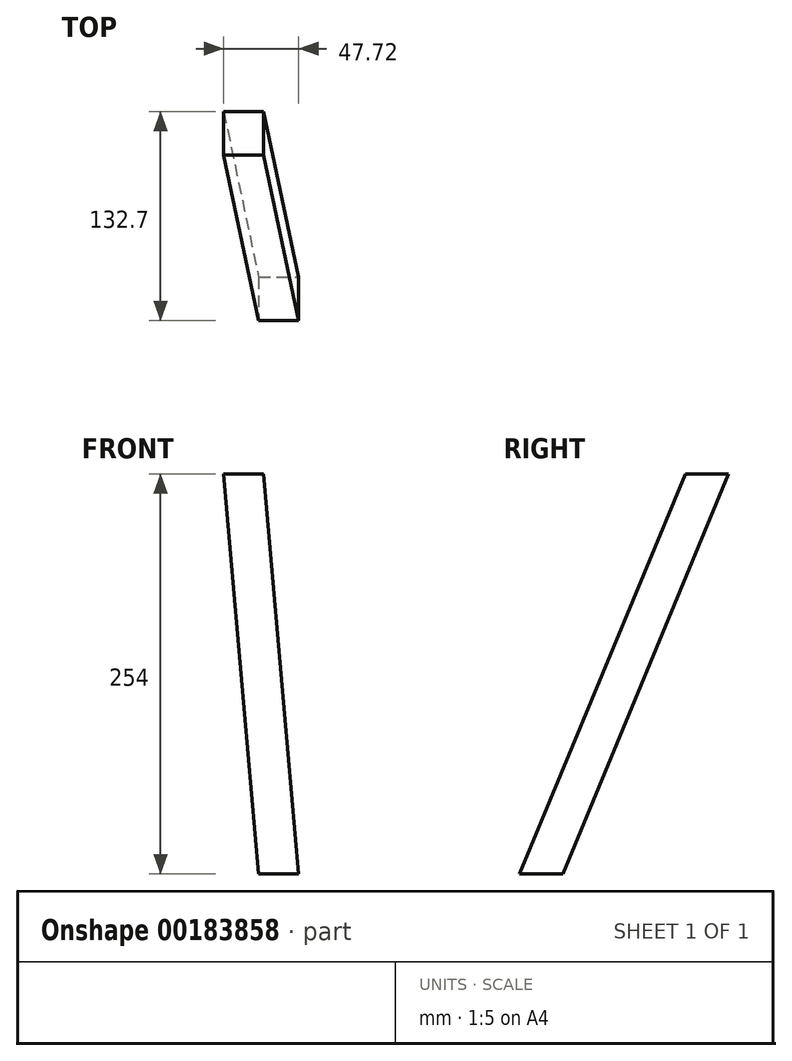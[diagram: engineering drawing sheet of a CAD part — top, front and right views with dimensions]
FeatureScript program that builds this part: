
annotation { "Feature Type Name" : "Feature", "Feature Type Description" : "" }
export const myFeature = defineFeature(function(context is Context, id is Id, definition is map)
    precondition{}
    {
        {
            var Q0;
            Q0=qCreatedBy(makeId("Front.planeOp"),FACE);
            var sketch = newSketch(context, id + "F0", { "sketchPlane" : qUnion([Q0])});
            skLineSegment(sketch, "E0.bottom", {"start": v(0, 0) * mm, "end": v(185.66, 0) * mm});
            skLineSegment(sketch, "E0.top", {"start": v(0, 254) * mm, "end": v(185.66, 254) * mm});
            skLineSegment(sketch, "E0.left", {"start": v(0, 0) * mm, "end": v(0, 254) * mm});
            skLineSegment(sketch, "E0.right", {"start": v(185.66, 0) * mm, "end": v(185.66, 254) * mm});
            skSolve(sketch);
        }
        {
            var Q0;
            Q0=makeQuery(id+"F0.imprint","IMPRINT",FACE,{"disambiguationData":[TD([[makeQuery(id+"F0.imprint","IMPRINT",EDGE,{"derivedFrom":sQuery(id+"F0.wireOp",EDGE,"E0.bottom")}),1.0]])]});
            extrude(context, id + "F1", {"entities" : qUnion([Q0]), "depth" : 254 * mm});
        }
        {
            var Q0;
            Q0=makeQuery(id+"F1.opExtrude","CAP_FACE",FACE,{"disambiguationData":[OSD([sQuery(id+"F0.wireOp",EDGE,"E0.bottom"),sQuery(id+"F0.wireOp",EDGE,"E0.top"),sQuery(id+"F0.wireOp",EDGE,"E0.left"),sQuery(id+"F0.wireOp",EDGE,"E0.right")])],"isStart":false});
            var sketch = newSketch(context, id + "F2", { "sketchPlane" : qUnion([Q0])});
            skLineSegment(sketch, "E1", {"start": v(0, 1743.05) * mm, "end": v(152.5, 0) * mm});
            skLineSegment(sketch, "E2", {"start": v(0, 1451.62) * mm, "end": v(127, 0) * mm});
            skSolve(sketch);
        }
        {
            var Q0;
            {var subQ5=makeQuery(id+"F1.opExtrude","CAP_EDGE",EDGE,{"disambiguationData":[OSD([sQuery(id+"F0.wireOp",EDGE,"E0.left")])],"isStart":false});Q0=makeQuery(id+"F2.imprint","IMPRINT",FACE,{"disambiguationData":[TD([[makeQuery(id+"F2.imprint","IMPRINT",EDGE,{"derivedFrom":subQ5}),-1.0]])]});}
            extrude(context, id + "F3", {"entities" : qUnion([Q0]), "operationType" : NewBodyOperationType.REMOVE, "endBound" : BoundingType.THROUGH_ALL, "oppositeDirection" : true, "depth" : 25.4 * mm});
        }
        {
            var Q0;
            Q0=makeQuery(id+"F1.opExtrude","SWEPT_FACE",FACE,{"disambiguationData":[OSD([sQuery(id+"F0.wireOp",EDGE,"E0.right")])]});
            var sketch = newSketch(context, id + "F4", { "sketchPlane" : qUnion([Q0])});
            skLineSegment(sketch, "E3", {"start": v(-254, 0) * mm, "end": v(-148.79, 254) * mm});
            skLineSegment(sketch, "E4", {"start": v(-226.5, 0) * mm, "end": v(-121.3, 254) * mm});
            skSolve(sketch);
        }
        {
            var Q0;
            {var subQ0=sQuery(id+"F4.wireOp",EDGE,"E3");Q0=makeQuery(id+"F4.imprint","IMPRINT",FACE,{"disambiguationData":[TD([[makeQuery(id+"F4.imprint","IMPRINT",EDGE,{"derivedFrom":subQ0}),1.0]])]});}
            extrude(context, id + "F5", {"entities" : qUnion([Q0]), "operationType" : NewBodyOperationType.REMOVE, "endBound" : BoundingType.THROUGH_ALL, "oppositeDirection" : true, "depth" : 25.4 * mm});
        }
        {
            var Q0;
            {var subQ0=sQuery(id+"F4.wireOp",EDGE,"E4");Q0=makeQuery(id+"F4.imprint","IMPRINT",FACE,{"disambiguationData":[TD([[makeQuery(id+"F4.imprint","IMPRINT",EDGE,{"derivedFrom":subQ0}),-1.0]])]});}
            extrude(context, id + "F6", {"entities" : qUnion([Q0]), "operationType" : NewBodyOperationType.REMOVE, "endBound" : BoundingType.THROUGH_ALL, "oppositeDirection" : true, "depth" : 25.4 * mm});
        }
        {
            var Q0;
            {var subQ5=makeQuery(id+"F1.opExtrude","CAP_EDGE",EDGE,{"disambiguationData":[OSD([sQuery(id+"F0.wireOp",EDGE,"E0.right")])],"isStart":false});Q0=makeQuery(id+"F2.imprint","IMPRINT",FACE,{"disambiguationData":[TD([[makeQuery(id+"F2.imprint","IMPRINT",EDGE,{"derivedFrom":subQ5}),1.0]])]});}
            extrude(context, id + "F7", {"entities" : qUnion([Q0]), "operationType" : NewBodyOperationType.REMOVE, "endBound" : BoundingType.THROUGH_ALL, "oppositeDirection" : true, "depth" : 25.4 * mm});
        }
        {
            var Q0;
            {var subQ0=sQuery(id+"F0.wireOp",EDGE,"E0.bottom");Q0=makeQuery(id+"F5.boolean.opBoolean","MERGE",EDGE,{"derivedFrom":[makeQuery(id+"F1.opExtrude","CAP_EDGE",EDGE,{"disambiguationData":[OSD([subQ0])],"isStart":false}),makeQuery(id+"F5.opExtrude","SWEPT_EDGE",EDGE,{"disambiguationData":[OSD([subQ0,sQuery(id+"F0.wireOp",EDGE,"E0.right"),sQuery(id+"F4.wireOp",EDGE,"E3")])]})]});}
            cPoint(context, id + "F8", {"entities" : qUnion([Q0]), "parameter" : 0.5});
        }
        {
            var Q0;
            Q0=makeQuery(id+"F7.boolean.opBoolean","INTERSECT",EDGE,{"derivedFrom":[makeQuery(id+"F5.boolean.opBoolean","COPY",FACE,{"derivedFrom":makeQuery(id+"F5.opExtrude","SWEPT_FACE",FACE,{"disambiguationData":[OSD([sQuery(id+"F4.wireOp",EDGE,"E3")])]})}),makeQuery(id+"F7.opExtrude","SWEPT_FACE",FACE,{"disambiguationData":[OSD([sQuery(id+"F2.wireOp",EDGE,"E1")])]})]});
            var Q1;
            Q1 = qCreatedBy(id + "F8" ,VERTEX);
            cPlane(context, id + "F9", {"entities" : qUnion([Q0, Q1]), "cplaneType" : CPlaneType.LINE_POINT, "offset" : 25.4 * mm, "width" : 152.4 * mm, "height" : 152.4 * mm});
        }
    });
